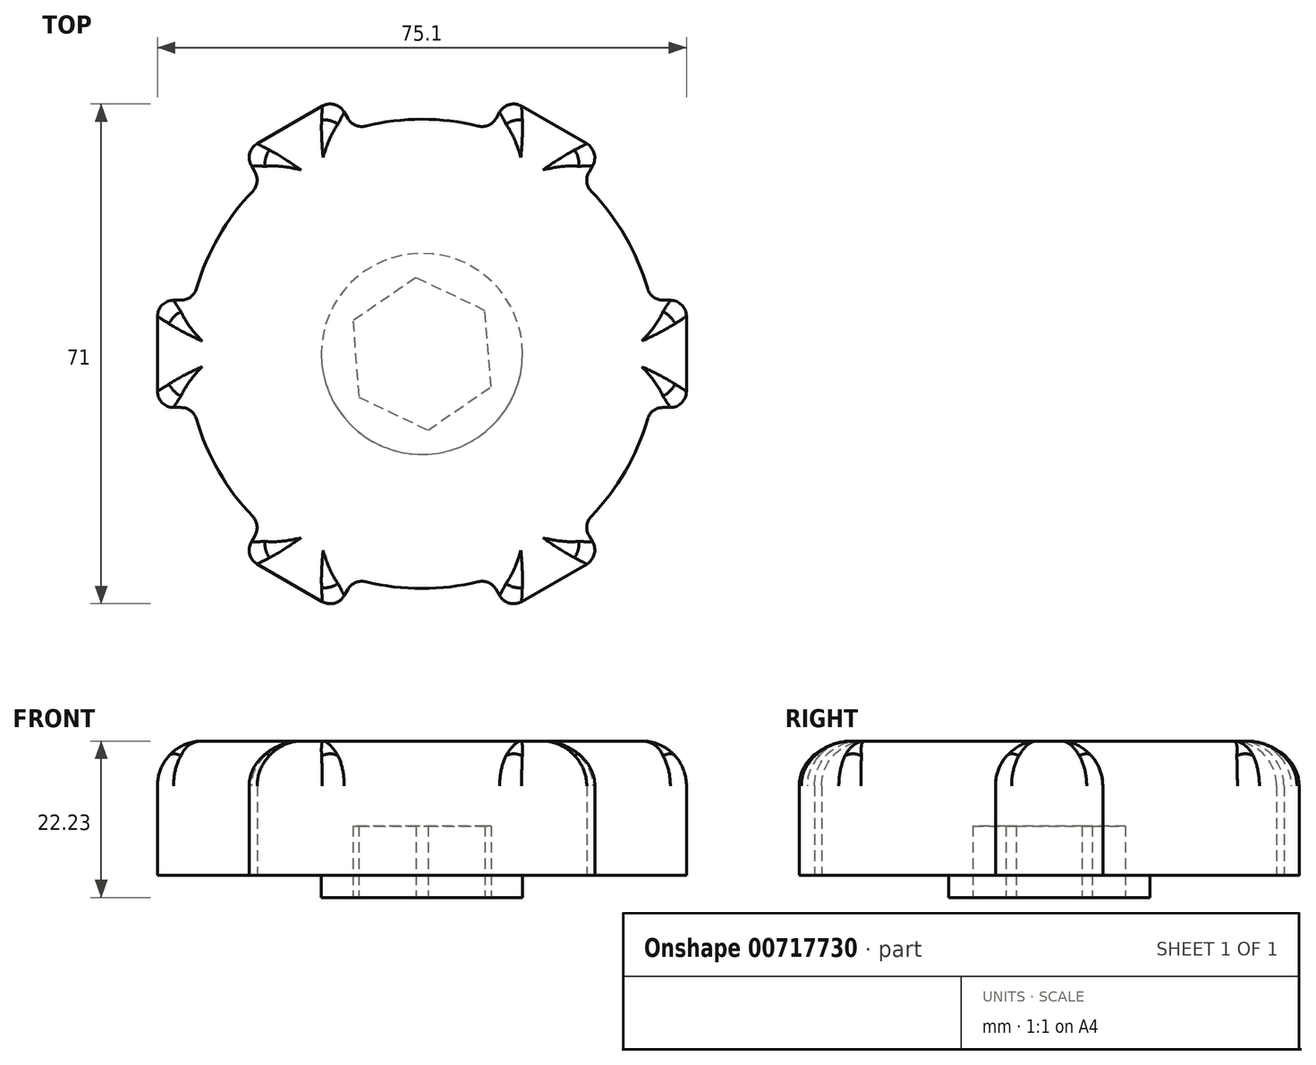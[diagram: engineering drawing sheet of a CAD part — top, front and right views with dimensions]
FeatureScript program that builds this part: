
annotation { "Feature Type Name" : "Feature", "Feature Type Description" : "" }
export const myFeature = defineFeature(function(context is Context, id is Id, definition is map)
    precondition{}
    {
        {
            var Q0;
            Q0=qCreatedBy(makeId("Top.planeOp"),FACE);
            var sketch = newSketch(context, id + "F0", { "sketchPlane" : qUnion([Q0])});
            skCircle(sketch, "E0", {"center": v(0, 0) * mm, "radius": 33.34 * mm});
            skLineSegment(sketch, "E1.bottom", {"start": v(37.55, 7.62) * mm, "end": v(-37.55, 7.62) * mm});
            skLineSegment(sketch, "E1.top", {"start": v(37.55, -7.62) * mm, "end": v(-37.55, -7.62) * mm});
            skLineSegment(sketch, "E1.left", {"start": v(37.55, 7.62) * mm, "end": v(37.55, -7.62) * mm});
            skLineSegment(sketch, "E1.right", {"start": v(-37.55, 7.62) * mm, "end": v(-37.55, -7.62) * mm});
            skLineSegment(sketch, "E2.1.0", {"start": v(-25.38, 28.71) * mm, "end": v(12.18, -36.33) * mm});
            skLineSegment(sketch, "E2.1.1", {"start": v(-25.38, 28.71) * mm, "end": v(-12.18, 36.33) * mm});
            skLineSegment(sketch, "E2.1.2", {"start": v(-12.18, 36.33) * mm, "end": v(25.38, -28.71) * mm});
            skLineSegment(sketch, "E2.1.4", {"start": v(12.18, -36.33) * mm, "end": v(25.38, -28.71) * mm});
            skLineSegment(sketch, "E2.2.0", {"start": v(-12.18, -36.33) * mm, "end": v(25.38, 28.71) * mm});
            skLineSegment(sketch, "E2.2.1", {"start": v(-12.18, -36.33) * mm, "end": v(-25.38, -28.71) * mm});
            skLineSegment(sketch, "E2.2.2", {"start": v(-25.38, -28.71) * mm, "end": v(12.18, 36.33) * mm});
            skLineSegment(sketch, "E2.2.4", {"start": v(25.38, 28.71) * mm, "end": v(12.18, 36.33) * mm});
            skSolve(sketch);
        }
        {
            var Q0;
            Q0 = qSketchRegion(id + "F0", true);
            var Q1;
            {var subQ0=sQuery(id+"F0.wireOp",EDGE,"E2.1.2");var subQ1=sQuery(id+"F0.wireOp",EDGE,"E1.bottom");var subQ2=makeQuery(id+"F0.imprint","INTERSECT",VERTEX,{"derivedFrom":[subQ1,subQ0]});Q1=makeQuery(id+"F0.imprint","IMPRINT",FACE,{"disambiguationData":[TD([[makeQuery(id+"F0.imprint","IMPRINT",EDGE,{"disambiguationData":[TD([[subQ2,-1.0]])],"derivedFrom":subQ1}),1.0]])]});}
            var Q2;
            {var subQ0=sQuery(id+"F0.wireOp",EDGE,"E2.2.2");var subQ1=sQuery(id+"F0.wireOp",EDGE,"E1.bottom");var subQ2=makeQuery(id+"F0.imprint","INTERSECT",VERTEX,{"derivedFrom":[subQ1,subQ0]});Q2=makeQuery(id+"F0.imprint","IMPRINT",FACE,{"disambiguationData":[TD([[makeQuery(id+"F0.imprint","IMPRINT",EDGE,{"disambiguationData":[TD([[subQ2,-1.0]])],"derivedFrom":subQ1}),1.0]])]});}
            var Q3;
            {var subQ0=sQuery(id+"F0.wireOp",EDGE,"E2.2.0");var subQ1=sQuery(id+"F0.wireOp",EDGE,"E1.bottom");var subQ2=makeQuery(id+"F0.imprint","INTERSECT",VERTEX,{"derivedFrom":[subQ1,subQ0]});Q3=makeQuery(id+"F0.imprint","IMPRINT",FACE,{"disambiguationData":[TD([[makeQuery(id+"F0.imprint","IMPRINT",EDGE,{"disambiguationData":[TD([[subQ2,-1.0]])],"derivedFrom":subQ1}),1.0]])]});}
            var Q4;
            {var subQ0=sQuery(id+"F0.wireOp",EDGE,"E2.1.2");var subQ1=sQuery(id+"F0.wireOp",EDGE,"E1.bottom");var subQ2=makeQuery(id+"F0.imprint","INTERSECT",VERTEX,{"derivedFrom":[subQ1,subQ0]});Q4=makeQuery(id+"F0.imprint","IMPRINT",FACE,{"disambiguationData":[TD([[makeQuery(id+"F0.imprint","IMPRINT",EDGE,{"disambiguationData":[TD([[subQ2,-1.0]])],"derivedFrom":subQ1}),-1.0]])]});}
            var Q5;
            {var subQ0=sQuery(id+"F0.wireOp",EDGE,"E2.1.2");var subQ1=sQuery(id+"F0.wireOp",EDGE,"E1.top");var subQ2=makeQuery(id+"F0.imprint","INTERSECT",VERTEX,{"derivedFrom":[subQ1,subQ0]});Q5=makeQuery(id+"F0.imprint","IMPRINT",FACE,{"disambiguationData":[TD([[makeQuery(id+"F0.imprint","IMPRINT",EDGE,{"disambiguationData":[TD([[subQ2,-1.0]])],"derivedFrom":subQ1}),-1.0]])]});}
            var Q6;
            {var subQ0=sQuery(id+"F0.wireOp",EDGE,"E2.2.0");var subQ1=sQuery(id+"F0.wireOp",EDGE,"E1.top");var subQ2=makeQuery(id+"F0.imprint","INTERSECT",VERTEX,{"derivedFrom":[subQ1,subQ0]});Q6=makeQuery(id+"F0.imprint","IMPRINT",FACE,{"disambiguationData":[TD([[makeQuery(id+"F0.imprint","IMPRINT",EDGE,{"disambiguationData":[TD([[subQ2,-1.0]])],"derivedFrom":subQ1}),1.0]])]});}
            var Q7;
            {var subQ0=sQuery(id+"F0.wireOp",EDGE,"E2.1.0");var subQ1=sQuery(id+"F0.wireOp",EDGE,"E1.top");var subQ2=makeQuery(id+"F0.imprint","INTERSECT",VERTEX,{"derivedFrom":[subQ1,subQ0]});Q7=makeQuery(id+"F0.imprint","IMPRINT",FACE,{"disambiguationData":[TD([[makeQuery(id+"F0.imprint","IMPRINT",EDGE,{"disambiguationData":[TD([[subQ2,-1.0]])],"derivedFrom":subQ1}),-1.0]])]});}
            extrude(context, id + "F1", {"entities" : qUnion([Q0, Q1, Q2, Q3, Q4, Q5, Q6, Q7]), "depth" : 19.05 * mm, "offsetDistance" : 25.4 * mm});
        }
        {
            var Q0;
            {var subQ0=sQuery(id+"F0.wireOp",EDGE,"E0");var subQ1=sQuery(id+"F0.wireOp",EDGE,"E2.2.0");Q0=makeQuery(id+"F1.opExtrude","SWEPT_EDGE",EDGE,{"disambiguationData":[OSD([subQ1,subQ0]),TDD([makeQuery(id+"F0.imprint","INTERSECT",VERTEX,{"disambiguationData":[OD(1.0)],"derivedFrom":[subQ1,subQ0]})])]});}
            var Q1;
            Q1=makeQuery(id+"F1.opExtrude","SWEPT_EDGE",EDGE,{"disambiguationData":[OSD([sQuery(id+"F0.wireOp",EDGE,"E2.2.0"),sQuery(id+"F0.wireOp",EDGE,"E2.2.4")])]});
            var Q2;
            Q2=makeQuery(id+"F1.opExtrude","SWEPT_EDGE",EDGE,{"disambiguationData":[OSD([sQuery(id+"F0.wireOp",EDGE,"E1.bottom"),sQuery(id+"F0.wireOp",EDGE,"E1.left")])]});
            var Q3;
            {var subQ0=sQuery(id+"F0.wireOp",EDGE,"E0");var subQ1=sQuery(id+"F0.wireOp",EDGE,"E1.bottom");Q3=makeQuery(id+"F1.opExtrude","SWEPT_EDGE",EDGE,{"disambiguationData":[OSD([subQ1,subQ0]),TDD([makeQuery(id+"F0.imprint","INTERSECT",VERTEX,{"disambiguationData":[OD(0.0)],"derivedFrom":[subQ1,subQ0]})])]});}
            var Q4;
            Q4=makeQuery(id+"F1.opExtrude","SWEPT_EDGE",EDGE,{"disambiguationData":[OSD([sQuery(id+"F0.wireOp",EDGE,"E1.top"),sQuery(id+"F0.wireOp",EDGE,"E1.left")])]});
            var Q5;
            {var subQ0=sQuery(id+"F0.wireOp",EDGE,"E0");var subQ1=sQuery(id+"F0.wireOp",EDGE,"E1.top");Q5=makeQuery(id+"F1.opExtrude","SWEPT_EDGE",EDGE,{"disambiguationData":[OSD([subQ1,subQ0]),TDD([makeQuery(id+"F0.imprint","INTERSECT",VERTEX,{"disambiguationData":[OD(0.0)],"derivedFrom":[subQ1,subQ0]})])]});}
            var Q6;
            Q6=makeQuery(id+"F1.opExtrude","SWEPT_EDGE",EDGE,{"disambiguationData":[OSD([sQuery(id+"F0.wireOp",EDGE,"E2.1.2"),sQuery(id+"F0.wireOp",EDGE,"E2.1.4")])]});
            var Q7;
            {var subQ0=sQuery(id+"F0.wireOp",EDGE,"E0");var subQ1=sQuery(id+"F0.wireOp",EDGE,"E2.1.2");Q7=makeQuery(id+"F1.opExtrude","SWEPT_EDGE",EDGE,{"disambiguationData":[OSD([subQ1,subQ0]),TDD([makeQuery(id+"F0.imprint","INTERSECT",VERTEX,{"disambiguationData":[OD(1.0)],"derivedFrom":[subQ1,subQ0]})])]});}
            var Q8;
            Q8=makeQuery(id+"F1.opExtrude","SWEPT_EDGE",EDGE,{"disambiguationData":[OSD([sQuery(id+"F0.wireOp",EDGE,"E2.1.0"),sQuery(id+"F0.wireOp",EDGE,"E2.1.4")])]});
            var Q9;
            {var subQ0=sQuery(id+"F0.wireOp",EDGE,"E0");var subQ1=sQuery(id+"F0.wireOp",EDGE,"E2.1.0");Q9=makeQuery(id+"F1.opExtrude","SWEPT_EDGE",EDGE,{"disambiguationData":[OSD([subQ1,subQ0]),TDD([makeQuery(id+"F0.imprint","INTERSECT",VERTEX,{"disambiguationData":[OD(1.0)],"derivedFrom":[subQ1,subQ0]})])]});}
            var Q10;
            {var subQ0=sQuery(id+"F0.wireOp",EDGE,"E0");var subQ1=sQuery(id+"F0.wireOp",EDGE,"E2.2.0");Q10=makeQuery(id+"F1.opExtrude","SWEPT_EDGE",EDGE,{"disambiguationData":[OSD([subQ1,subQ0]),TDD([makeQuery(id+"F0.imprint","INTERSECT",VERTEX,{"disambiguationData":[OD(0.0)],"derivedFrom":[subQ1,subQ0]})])]});}
            var Q11;
            Q11=makeQuery(id+"F1.opExtrude","SWEPT_EDGE",EDGE,{"disambiguationData":[OSD([sQuery(id+"F0.wireOp",EDGE,"E2.2.0"),sQuery(id+"F0.wireOp",EDGE,"E2.2.1")])]});
            var Q12;
            Q12=makeQuery(id+"F1.opExtrude","SWEPT_EDGE",EDGE,{"disambiguationData":[OSD([sQuery(id+"F0.wireOp",EDGE,"E2.2.1"),sQuery(id+"F0.wireOp",EDGE,"E2.2.2")])]});
            var Q13;
            {var subQ0=sQuery(id+"F0.wireOp",EDGE,"E0");var subQ1=sQuery(id+"F0.wireOp",EDGE,"E2.2.2");Q13=makeQuery(id+"F1.opExtrude","SWEPT_EDGE",EDGE,{"disambiguationData":[OSD([subQ1,subQ0]),TDD([makeQuery(id+"F0.imprint","INTERSECT",VERTEX,{"disambiguationData":[OD(0.0)],"derivedFrom":[subQ1,subQ0]})])]});}
            var Q14;
            {var subQ0=sQuery(id+"F0.wireOp",EDGE,"E0");var subQ1=sQuery(id+"F0.wireOp",EDGE,"E1.top");Q14=makeQuery(id+"F1.opExtrude","SWEPT_EDGE",EDGE,{"disambiguationData":[OSD([subQ1,subQ0]),TDD([makeQuery(id+"F0.imprint","INTERSECT",VERTEX,{"disambiguationData":[OD(1.0)],"derivedFrom":[subQ1,subQ0]})])]});}
            var Q15;
            Q15=makeQuery(id+"F1.opExtrude","SWEPT_EDGE",EDGE,{"disambiguationData":[OSD([sQuery(id+"F0.wireOp",EDGE,"E1.top"),sQuery(id+"F0.wireOp",EDGE,"E1.right")])]});
            var Q16;
            Q16=makeQuery(id+"F1.opExtrude","SWEPT_EDGE",EDGE,{"disambiguationData":[OSD([sQuery(id+"F0.wireOp",EDGE,"E1.bottom"),sQuery(id+"F0.wireOp",EDGE,"E1.right")])]});
            var Q17;
            {var subQ0=sQuery(id+"F0.wireOp",EDGE,"E0");var subQ1=sQuery(id+"F0.wireOp",EDGE,"E1.bottom");Q17=makeQuery(id+"F1.opExtrude","SWEPT_EDGE",EDGE,{"disambiguationData":[OSD([subQ1,subQ0]),TDD([makeQuery(id+"F0.imprint","INTERSECT",VERTEX,{"disambiguationData":[OD(1.0)],"derivedFrom":[subQ1,subQ0]})])]});}
            var Q18;
            {var subQ0=sQuery(id+"F0.wireOp",EDGE,"E0");var subQ1=sQuery(id+"F0.wireOp",EDGE,"E2.1.0");Q18=makeQuery(id+"F1.opExtrude","SWEPT_EDGE",EDGE,{"disambiguationData":[OSD([subQ1,subQ0]),TDD([makeQuery(id+"F0.imprint","INTERSECT",VERTEX,{"disambiguationData":[OD(0.0)],"derivedFrom":[subQ1,subQ0]})])]});}
            var Q19;
            Q19=makeQuery(id+"F1.opExtrude","SWEPT_EDGE",EDGE,{"disambiguationData":[OSD([sQuery(id+"F0.wireOp",EDGE,"E2.1.0"),sQuery(id+"F0.wireOp",EDGE,"E2.1.1")])]});
            var Q20;
            Q20=makeQuery(id+"F1.opExtrude","SWEPT_EDGE",EDGE,{"disambiguationData":[OSD([sQuery(id+"F0.wireOp",EDGE,"E2.1.1"),sQuery(id+"F0.wireOp",EDGE,"E2.1.2")])]});
            var Q21;
            {var subQ0=sQuery(id+"F0.wireOp",EDGE,"E0");var subQ1=sQuery(id+"F0.wireOp",EDGE,"E2.1.2");Q21=makeQuery(id+"F1.opExtrude","SWEPT_EDGE",EDGE,{"disambiguationData":[OSD([subQ1,subQ0]),TDD([makeQuery(id+"F0.imprint","INTERSECT",VERTEX,{"disambiguationData":[OD(0.0)],"derivedFrom":[subQ1,subQ0]})])]});}
            var Q22;
            {var subQ0=sQuery(id+"F0.wireOp",EDGE,"E0");var subQ1=sQuery(id+"F0.wireOp",EDGE,"E2.2.2");Q22=makeQuery(id+"F1.opExtrude","SWEPT_EDGE",EDGE,{"disambiguationData":[OSD([subQ1,subQ0]),TDD([makeQuery(id+"F0.imprint","INTERSECT",VERTEX,{"disambiguationData":[OD(1.0)],"derivedFrom":[subQ1,subQ0]})])]});}
            var Q23;
            Q23=makeQuery(id+"F1.opExtrude","SWEPT_EDGE",EDGE,{"disambiguationData":[OSD([sQuery(id+"F0.wireOp",EDGE,"E2.2.2"),sQuery(id+"F0.wireOp",EDGE,"E2.2.4")])]});
            fillet(context, id + "F2", {"entities" : qUnion([Q0, Q1, Q2, Q3, Q4, Q5, Q6, Q7, Q8, Q9, Q10, Q11, Q12, Q13, Q14, Q15, Q16, Q17, Q18, Q19, Q20, Q21, Q22, Q23]), "radius" : 2.3 * mm, "tangentPropagation" : true, "allowEdgeOverflow" : false});
        }
        {
            var Q0;
            Q0=makeQuery(id+"F1.opExtrude","CAP_FACE",FACE,{"disambiguationData":[OSD([sQuery(id+"F0.wireOp",EDGE,"E1.bottom"),sQuery(id+"F0.wireOp",EDGE,"E1.top"),sQuery(id+"F0.wireOp",EDGE,"E1.left"),sQuery(id+"F0.wireOp",EDGE,"E1.right"),sQuery(id+"F0.wireOp",EDGE,"E2.1.0"),sQuery(id+"F0.wireOp",EDGE,"E2.1.1"),sQuery(id+"F0.wireOp",EDGE,"E2.1.2"),sQuery(id+"F0.wireOp",EDGE,"E2.1.4"),sQuery(id+"F0.wireOp",EDGE,"E2.2.0"),sQuery(id+"F0.wireOp",EDGE,"E2.2.1"),sQuery(id+"F0.wireOp",EDGE,"E2.2.2"),sQuery(id+"F0.wireOp",EDGE,"E0"),sQuery(id+"F0.wireOp",EDGE,"E2.2.4")])],"isStart":false});
            fillet(context, id + "F3", {"entities" : qUnion([Q0]), "radius" : 6.35 * mm, "tangentPropagation" : true, "allowEdgeOverflow" : false});
        }
        {
            var Q0;
            Q0=makeQuery(id+"F1.opExtrude","CAP_FACE",FACE,{"disambiguationData":[OSD([sQuery(id+"F0.wireOp",EDGE,"E1.bottom"),sQuery(id+"F0.wireOp",EDGE,"E1.top"),sQuery(id+"F0.wireOp",EDGE,"E1.left"),sQuery(id+"F0.wireOp",EDGE,"E1.right"),sQuery(id+"F0.wireOp",EDGE,"E2.1.0"),sQuery(id+"F0.wireOp",EDGE,"E2.1.1"),sQuery(id+"F0.wireOp",EDGE,"E2.1.2"),sQuery(id+"F0.wireOp",EDGE,"E2.1.4"),sQuery(id+"F0.wireOp",EDGE,"E2.2.0"),sQuery(id+"F0.wireOp",EDGE,"E2.2.1"),sQuery(id+"F0.wireOp",EDGE,"E2.2.2"),sQuery(id+"F0.wireOp",EDGE,"E0"),sQuery(id+"F0.wireOp",EDGE,"E2.2.4")])],"isStart":true});
            var sketch = newSketch(context, id + "F4", { "sketchPlane" : qUnion([Q0])});
            skSolve(sketch);
        }
        {
            var Q0;
            {var subQ23=sQuery(id+"F0.wireOp",EDGE,"E1.left");Q0=makeQuery(id+"F4.imprint","IMPRINT",FACE,{"disambiguationData":[TD([[makeQuery(id+"F4.imprint","IMPRINT",EDGE,{"derivedFrom":makeQuery(id+"F1.opExtrude","CAP_EDGE",EDGE,{"disambiguationData":[OSD([subQ23])],"isStart":true})}),1.0]])]});}
            var sketch = newSketch(context, id + "F5", { "sketchPlane" : qUnion([Q0])});
            skCircle(sketch, "E3", {"center": v(0, 0) * mm, "radius": 14.29 * mm});
            skSolve(sketch);
        }
        {
            var Q0;
            Q0 = qSketchRegion(id + "F5", true);
            extrude(context, id + "F6", {"entities" : qUnion([Q0]), "operationType" : NewBodyOperationType.ADD, "depth" : 3.17 * mm, "offsetDistance" : 25.4 * mm});
        }
        {
            var Q0;
            Q0=makeQuery(id+"F6.opExtrude","CAP_FACE",FACE,{"disambiguationData":[OSD([sQuery(id+"F5.wireOp",EDGE,"E3")])],"isStart":false});
            var sketch = newSketch(context, id + "F7", { "sketchPlane" : qUnion([Q0])});
            skCircle(sketch, "E4.cCircle", {"center": v(0, 0) * mm, "radius": 9.41 * mm, "construction": true});
            skLineSegment(sketch, "E4.0", {"start": v(8.96, -6.15) * mm, "end": v(-0.85, -10.83) * mm});
            skLineSegment(sketch, "E4.1", {"start": v(-0.85, -10.83) * mm, "end": v(-9.8, -4.68) * mm});
            skLineSegment(sketch, "E4.2", {"start": v(-9.8, -4.68) * mm, "end": v(-8.96, 6.15) * mm});
            skLineSegment(sketch, "E4.3", {"start": v(-8.96, 6.15) * mm, "end": v(0.85, 10.83) * mm});
            skLineSegment(sketch, "E4.4", {"start": v(0.85, 10.83) * mm, "end": v(9.8, 4.68) * mm});
            skLineSegment(sketch, "E4.5", {"start": v(9.8, 4.68) * mm, "end": v(8.96, -6.15) * mm});
            skPoint(sketch, "E4.0.midPoint", {"position": v(4.05, -8.5) * mm});
            skSolve(sketch);
        }
        {
            var Q0;
            Q0 = qSketchRegion(id + "F7", true);
            extrude(context, id + "F8", {"entities" : qUnion([Q0]), "operationType" : NewBodyOperationType.REMOVE, "oppositeDirection" : true, "depth" : 10.16 * mm, "offsetDistance" : 25.4 * mm});
        }
    });
